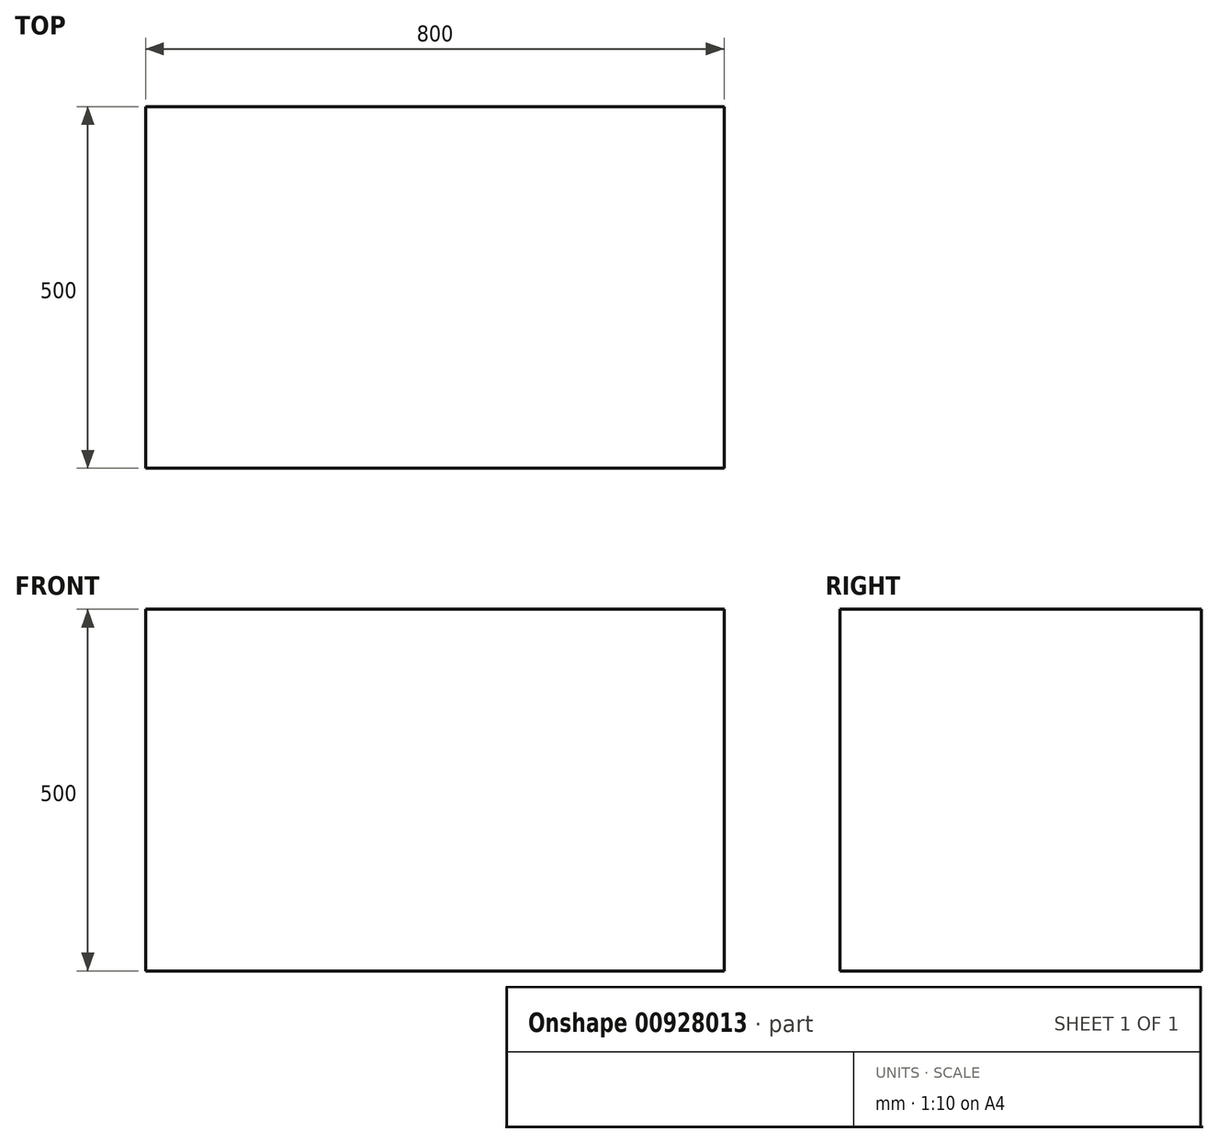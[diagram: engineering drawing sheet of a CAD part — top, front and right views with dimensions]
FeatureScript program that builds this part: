
annotation { "Feature Type Name" : "Feature", "Feature Type Description" : "" }
export const myFeature = defineFeature(function(context is Context, id is Id, definition is map)
    precondition{}
    {
        {
            var Q0;
            Q0=qCreatedBy(makeId("Front.planeOp"),FACE);
            var sketch = newSketch(context, id + "F0", { "sketchPlane" : qUnion([Q0])});
            skLineSegment(sketch, "E0.bottom", {"start": v(0, 0) * mm, "end": v(800, 0) * mm});
            skLineSegment(sketch, "E0.top", {"start": v(0, 500) * mm, "end": v(800, 500) * mm});
            skLineSegment(sketch, "E0.left", {"start": v(0, 0) * mm, "end": v(0, 500) * mm});
            skLineSegment(sketch, "E0.right", {"start": v(800, 0) * mm, "end": v(800, 500) * mm});
            skSolve(sketch);
        }
        {
            var Q0;
            Q0 = qSketchRegion(id + "F0", true);
            extrude(context, id + "F1", {"entities" : qUnion([Q0]), "oppositeDirection" : true, "depth" : 500 * mm, "offsetDistance" : 25 * mm});
        }
    });
